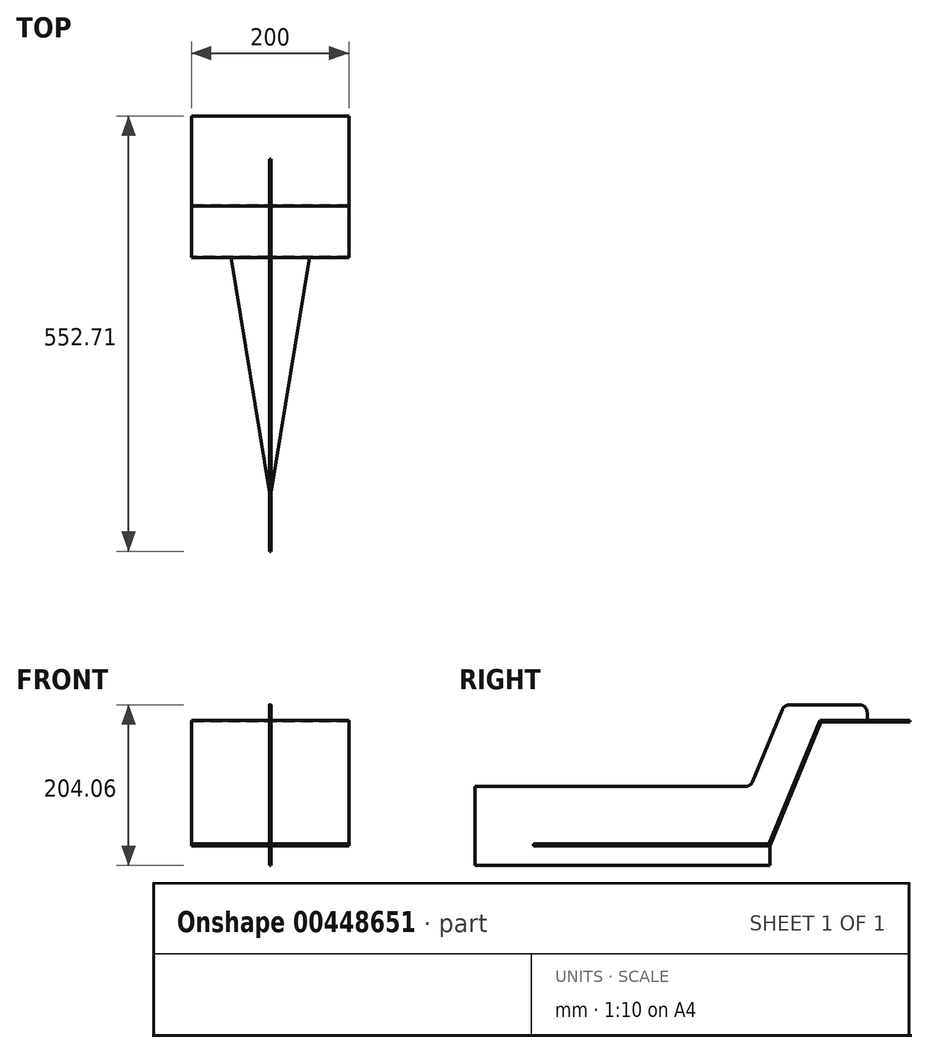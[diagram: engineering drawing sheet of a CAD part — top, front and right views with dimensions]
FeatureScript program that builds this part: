
annotation { "Feature Type Name" : "Feature", "Feature Type Description" : "" }
export const myFeature = defineFeature(function(context is Context, id is Id, definition is map)
    precondition{}
    {
        {
            var Q0;
            Q0=qCreatedBy(makeId("Right.planeOp"),FACE);
            var sketch = newSketch(context, id + "F0", { "sketchPlane" : qUnion([Q0])});
            skLineSegment(sketch, "E0", {"start": v(0, 0) * mm, "end": v(-300, 0) * mm});
            skLineSegment(sketch, "E1", {"start": v(-300, 0) * mm, "end": v(-300, 2) * mm});
            skLineSegment(sketch, "E2", {"start": v(-300, 2) * mm, "end": v(-1.34, 2) * mm});
            skLineSegment(sketch, "E3", {"start": v(0, 0) * mm, "end": v(65.06, 157.06) * mm});
            skLineSegment(sketch, "E4", {"start": v(65.06, 157.06) * mm, "end": v(178.06, 157.06) * mm});
            skLineSegment(sketch, "E5", {"start": v(178.06, 157.06) * mm, "end": v(178.06, 159.06) * mm});
            skLineSegment(sketch, "E6", {"start": v(178.06, 159.06) * mm, "end": v(63.72, 159.06) * mm});
            skLineSegment(sketch, "E7.0", {"start": v(-1.34, 2) * mm, "end": v(63.2, 157.82) * mm});
            skPoint(sketch, "E8.orphan", {"position": v(0, 2) * mm});
            skLineSegment(sketch, "E9", {"start": v(63.2, 157.82) * mm, "end": v(63.72, 159.06) * mm});
            skSolve(sketch);
        }
        {
            var Q0;
            Q0 = qSketchRegion(id + "F0", true);
            extrude(context, id + "F1", {"entities" : qUnion([Q0]), "endBound" : BoundingType.SYMMETRIC, "depth" : 200 * mm});
        }
        {
            var Q0;
            Q0=makeQuery(id+"F1.opExtrude","SWEPT_FACE",FACE,{"disambiguationData":[OSD([sQuery(id+"F0.wireOp",EDGE,"E2")])]});
            var sketch = newSketch(context, id + "F2", { "sketchPlane" : qUnion([Q0])});
            skLineSegment(sketch, "E10", {"start": v(-100, -1.34) * mm, "end": v(-50, -1.34) * mm});
            skLineSegment(sketch, "E11", {"start": v(-50, -1.34) * mm, "end": v(-1, -300) * mm});
            skLineSegment(sketch, "E12", {"start": v(-1, -300) * mm, "end": v(-100, -300) * mm});
            skLineSegment(sketch, "E13", {"start": v(-100, -300) * mm, "end": v(-100, -1.34) * mm});
            skLineSegment(sketch, "E14.MirrorCS", {"start": v(100, -1.34) * mm, "end": v(50, -1.34) * mm});
            skLineSegment(sketch, "E15.MirrorCS", {"start": v(1, -300) * mm, "end": v(100, -300) * mm});
            skLineSegment(sketch, "E16.MirrorCS", {"start": v(50, -1.34) * mm, "end": v(1, -300) * mm});
            skLineSegment(sketch, "E17.MirrorCS", {"start": v(100, -300) * mm, "end": v(100, -1.34) * mm});
            skSolve(sketch);
        }
        {
            var Q0;
            Q0 = qSketchRegion(id + "F2", true);
            extrude(context, id + "F3", {"entities" : qUnion([Q0]), "operationType" : NewBodyOperationType.REMOVE, "oppositeDirection" : true, "depth" : 2 * mm});
        }
        {
            var Q0;
            Q0=makeQuery(id+"F1.opExtrude","SWEPT_FACE",FACE,{"disambiguationData":[OSD([sQuery(id+"F0.wireOp",EDGE,"E2")])]});
            var sketch = newSketch(context, id + "F4", { "sketchPlane" : qUnion([Q0])});
            skLineSegment(sketch, "E18.bottom", {"start": v(1, -300) * mm, "end": v(-1, -300) * mm});
            skLineSegment(sketch, "E18.top", {"start": v(1, -1.34) * mm, "end": v(-1, -1.34) * mm});
            skLineSegment(sketch, "E18.left", {"start": v(1, -300) * mm, "end": v(1, -1.34) * mm});
            skLineSegment(sketch, "E18.right", {"start": v(-1, -300) * mm, "end": v(-1, -1.34) * mm});
            skSolve(sketch);
        }
        {
            var Q0;
            Q0=makeQuery(id+"F4.imprint","IMPRINT",FACE,{"disambiguationData":[TD([[makeQuery(id+"F4.imprint","IMPRINT",EDGE,{"derivedFrom":sQuery(id+"F4.wireOp",EDGE,"E18.bottom")}),-1.0]])]});
            extrude(context, id + "F5", {"entities" : qUnion([Q0]), "operationType" : NewBodyOperationType.REMOVE, "oppositeDirection" : true, "depth" : 2 * mm});
        }
        {
            var Q0;
            Q0=qCreatedBy(makeId("Right.planeOp"),FACE);
            var sketch = newSketch(context, id + "F6", { "sketchPlane" : qUnion([Q0])});
            skLineSegment(sketch, "E19", {"start": v(0, 0) * mm, "end": v(0, -25) * mm});
            skLineSegment(sketch, "E20", {"start": v(0, -25) * mm, "end": v(-374.65, -25) * mm});
            skLineSegment(sketch, "E21", {"start": v(-374.65, -25) * mm, "end": v(-374.65, 75) * mm});
            skLineSegment(sketch, "E22", {"start": v(-374.65, 75) * mm, "end": v(-31.33, 75) * mm});
            skLineSegment(sketch, "E23", {"start": v(-22.1, 81.17) * mm, "end": v(15.9, 172.89) * mm});
            skLineSegment(sketch, "E24", {"start": v(25.13, 179.06) * mm, "end": v(113.72, 179.06) * mm});
            skLineSegment(sketch, "E25", {"start": v(123.72, 169.06) * mm, "end": v(123.72, 159.06) * mm});
            skLineSegment(sketch, "E26", {"start": v(123.72, 159.06) * mm, "end": v(63.72, 159.06) * mm});
            skLineSegment(sketch, "E27", {"start": v(63.72, 159.06) * mm, "end": v(-1.32, 2) * mm});
            skLineSegment(sketch, "E28", {"start": v(-1.32, 2) * mm, "end": v(-1.32, 0) * mm});
            skLineSegment(sketch, "E29", {"start": v(0, 0) * mm, "end": v(-1.32, 0) * mm});
            skPoint(sketch, "E30.visualSharp", {"position": v(-24.65, 75) * mm});
            skArc(sketch, "E30.filletArc", {"start": v(-31.33, 75) * mm, "mid": v(-25.78, 76.69) * mm, "end": v(-22.1, 81.17) * mm});
            skPoint(sketch, "E31.visualSharp", {"position": v(18.45, 179.06) * mm});
            skArc(sketch, "E31.filletArc", {"start": v(25.13, 179.06) * mm, "mid": v(19.58, 177.37) * mm, "end": v(15.9, 172.89) * mm});
            skPoint(sketch, "E32.visualSharp", {"position": v(123.72, 179.06) * mm});
            skArc(sketch, "E32.filletArc", {"start": v(123.72, 169.06) * mm, "mid": v(120.8, 176.13) * mm, "end": v(113.72, 179.06) * mm});
            skSolve(sketch);
        }
        {
            var Q0;
            Q0=makeQuery(id+"F6.imprint","IMPRINT",FACE,{"disambiguationData":[TD([[makeQuery(id+"F6.imprint","IMPRINT",EDGE,{"derivedFrom":sQuery(id+"F6.wireOp",EDGE,"E19")}),-1.0]])]});
            extrude(context, id + "F7", {"entities" : qUnion([Q0]), "operationType" : NewBodyOperationType.ADD, "endBound" : BoundingType.SYMMETRIC, "depth" : 2 * mm});
        }
    });
